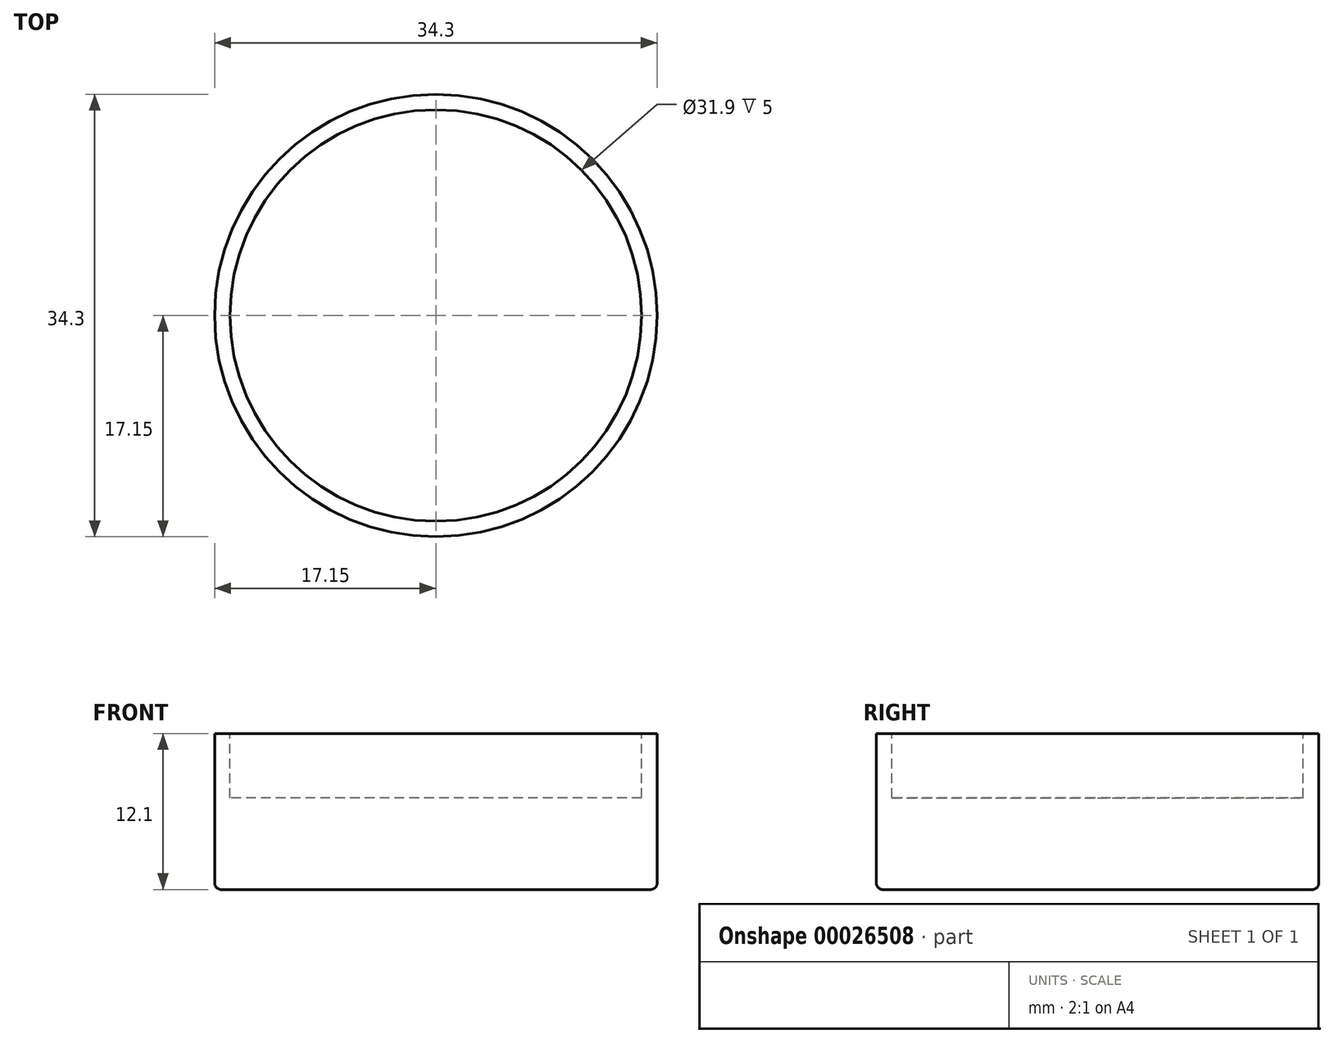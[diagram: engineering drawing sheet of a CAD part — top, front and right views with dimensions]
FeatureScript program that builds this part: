
annotation { "Feature Type Name" : "Feature", "Feature Type Description" : "" }
export const myFeature = defineFeature(function(context is Context, id is Id, definition is map)
    precondition{}
    {
        {
            var Q0;
            Q0=qCreatedBy(makeId("Top.planeOp"),FACE);
            var sketch = newSketch(context, id + "F0", { "sketchPlane" : qUnion([Q0])});
            skCircle(sketch, "E0", {"center": v(0, 0) * mm, "radius": 17.15 * mm});
            skSolve(sketch);
        }
        {
            var Q0;
            Q0=makeQuery(id+"F0.imprint","IMPRINT",FACE,{"disambiguationData":[TD([[makeQuery(id+"F0.imprint","IMPRINT",EDGE,{"derivedFrom":sQuery(id+"F0.wireOp",EDGE,"E0")}),1.0]])]});
            extrude(context, id + "F1", {"entities" : qUnion([Q0]), "depth" : 12.1 * mm});
        }
        {
            var Q0;
            Q0=makeQuery(id+"F1.opExtrude","CAP_FACE",FACE,{"disambiguationData":[OSD([sQuery(id+"F0.wireOp",EDGE,"E0")])],"isStart":false});
            var sketch = newSketch(context, id + "F2", { "sketchPlane" : qUnion([Q0])});
            skCircle(sketch, "E1", {"center": v(0, 0) * mm, "radius": 15.95 * mm});
            skSolve(sketch);
        }
        {
            var Q0;
            Q0=makeQuery(id+"F2.imprint","IMPRINT",FACE,{"disambiguationData":[TD([[makeQuery(id+"F2.imprint","IMPRINT",EDGE,{"derivedFrom":sQuery(id+"F2.wireOp",EDGE,"E1")}),1.0]])]});
            extrude(context, id + "F3", {"entities" : qUnion([Q0]), "operationType" : NewBodyOperationType.REMOVE, "oppositeDirection" : true, "depth" : 5 * mm});
        }
        {
            var Q0;
            Q0=makeQuery(id+"F1.opExtrude","CAP_EDGE",EDGE,{"disambiguationData":[OSD([sQuery(id+"F0.wireOp",EDGE,"E0")])],"isStart":true});
            fillet(context, id + "F4", {"entities" : qUnion([Q0]), "radius" : .5 * mm, "tangentPropagation" : true, "allowEdgeOverflow" : false});
        }
    });
